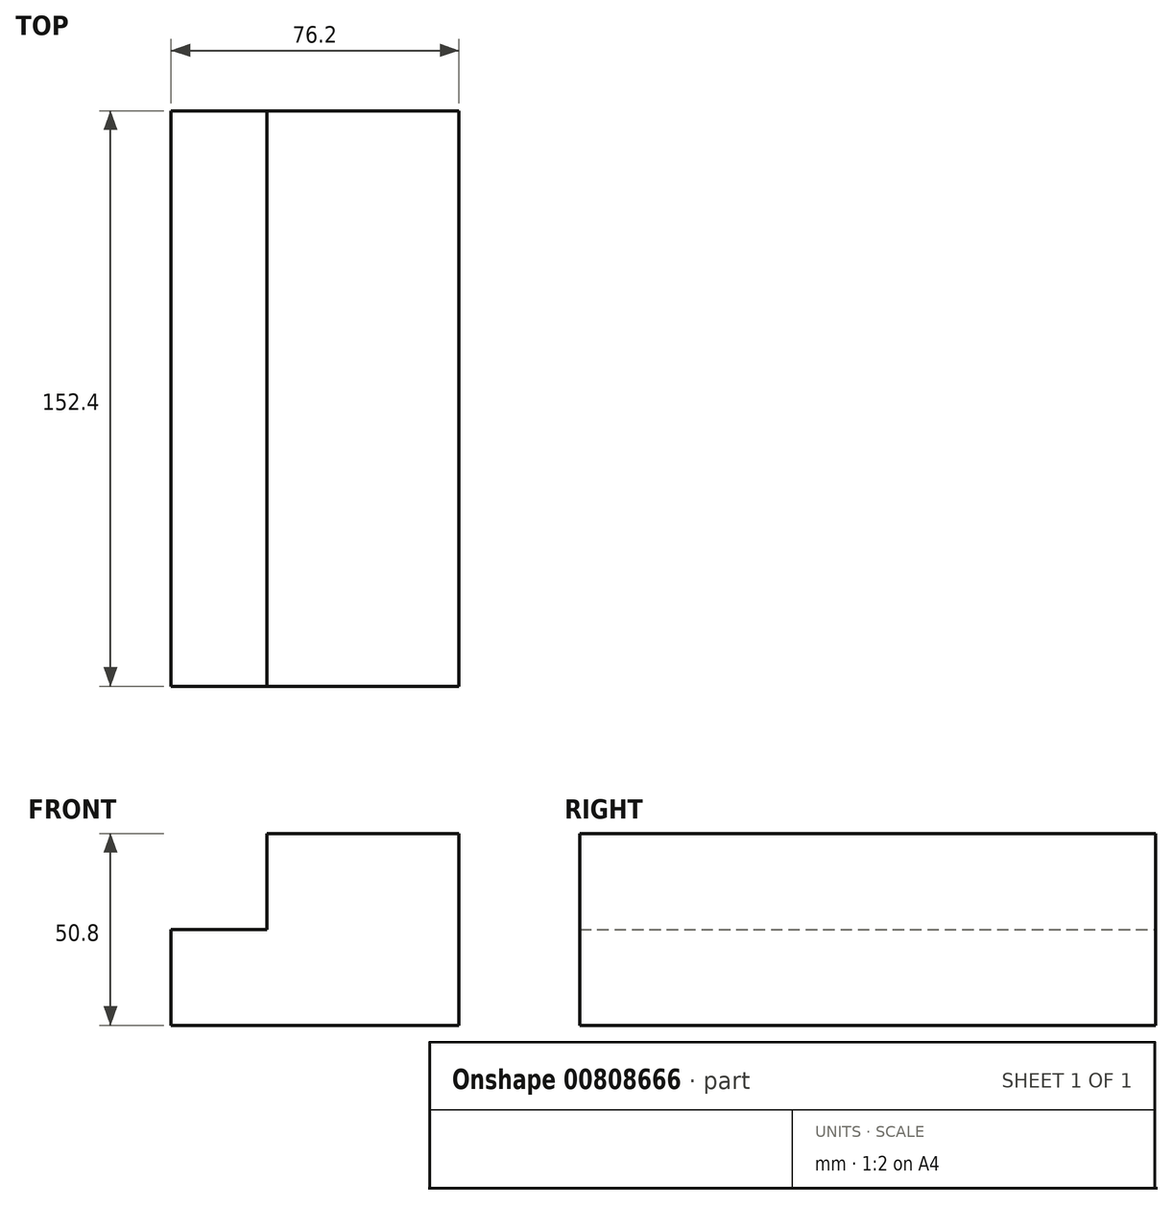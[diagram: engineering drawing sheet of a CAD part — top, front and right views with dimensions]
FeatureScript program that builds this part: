
annotation { "Feature Type Name" : "Feature", "Feature Type Description" : "" }
export const myFeature = defineFeature(function(context is Context, id is Id, definition is map)
    precondition{}
    {
        {
            var Q0;
            Q0=qCreatedBy(makeId("Front.planeOp"),FACE);
            var sketch = newSketch(context, id + "F0", { "sketchPlane" : qUnion([Q0])});
            skLineSegment(sketch, "E0", {"start": v(0, 0) * mm, "end": v(76.2, 0) * mm});
            skLineSegment(sketch, "E1", {"start": v(76.2, 0) * mm, "end": v(76.2, 50.8) * mm});
            skLineSegment(sketch, "E2", {"start": v(76.2, 50.8) * mm, "end": v(25.4, 50.8) * mm});
            skLineSegment(sketch, "E3", {"start": v(25.4, 50.8) * mm, "end": v(25.4, 25.4) * mm});
            skLineSegment(sketch, "E4", {"start": v(25.4, 25.4) * mm, "end": v(0, 25.4) * mm});
            skLineSegment(sketch, "E5", {"start": v(0, 25.4) * mm, "end": v(0, 0) * mm});
            skSolve(sketch);
        }
        {
            var Q0;
            Q0 = qSketchRegion(id + "F0", true);
            extrude(context, id + "F1", {"entities" : qUnion([Q0]), "depth" : 152.4 * mm, "offsetDistance" : 25.4 * mm});
        }
    });
